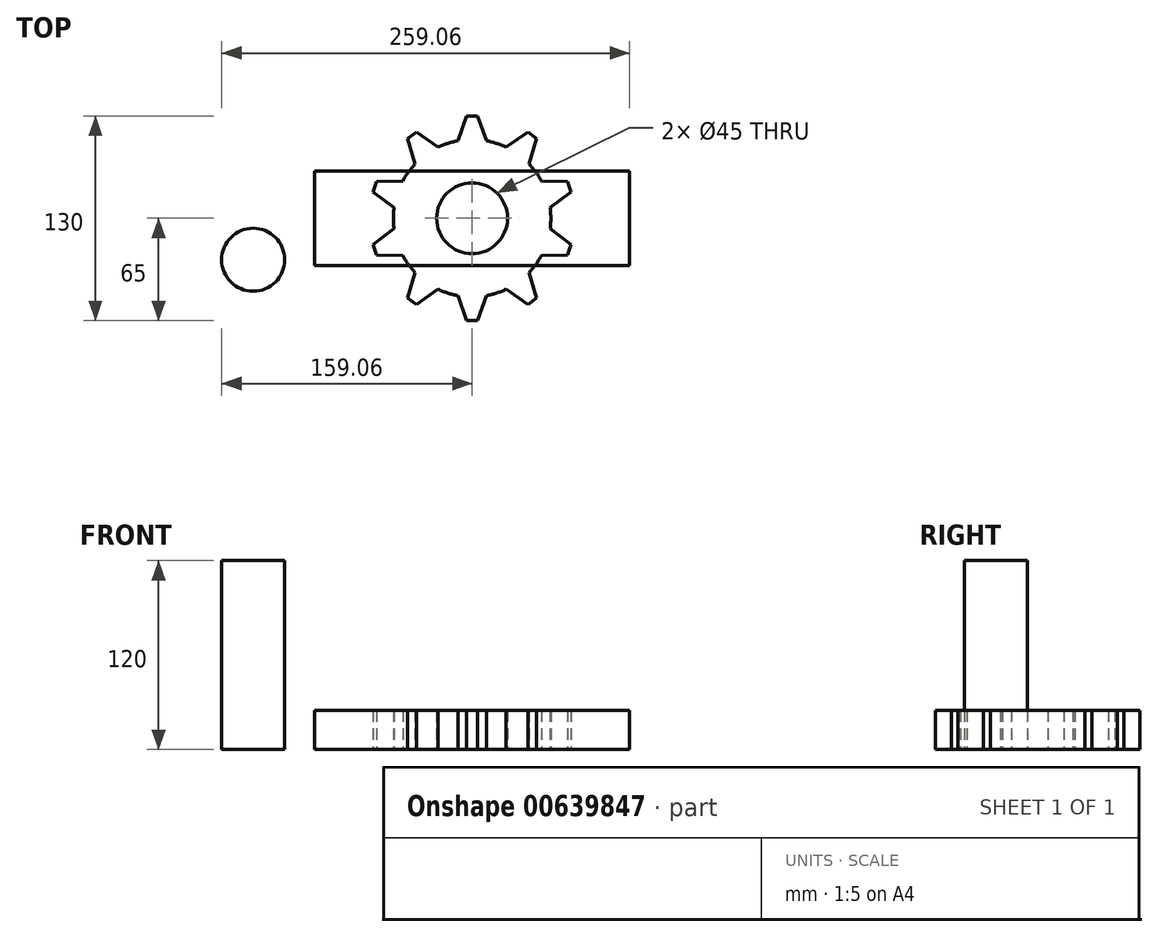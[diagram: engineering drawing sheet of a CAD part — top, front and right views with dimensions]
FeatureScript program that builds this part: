
annotation { "Feature Type Name" : "Feature", "Feature Type Description" : "" }
export const myFeature = defineFeature(function(context is Context, id is Id, definition is map)
    precondition{}
    {
        {
            var Q0;
            Q0=qCreatedBy(makeId("Top.planeOp"),FACE);
            var sketch = newSketch(context, id + "F0", { "sketchPlane" : qUnion([Q0])});
            skCircle(sketch, "E0", {"center": v(0, 0) * mm, "radius": 50 * mm});
            skLineSegment(sketch, "E1", {"start": v(0, 0) * mm, "end": v(0, 80) * mm, "construction": true});
            skLineSegment(sketch, "E2", {"start": v(0, 65) * mm, "end": v(3.5, 65) * mm});
            skLineSegment(sketch, "E3", {"start": v(3.5, 65) * mm, "end": v(9, 49.18) * mm});
            skLineSegment(sketch, "E4.MirrorCS", {"start": v(0, 65) * mm, "end": v(-3.5, 65) * mm});
            skLineSegment(sketch, "E5.MirrorCS", {"start": v(-3.5, 65) * mm, "end": v(-9, 49.18) * mm});
            skLineSegment(sketch, "E6.1.0", {"start": v(-41.04, 50.53) * mm, "end": v(-36.2, 34.5) * mm});
            skLineSegment(sketch, "E6.1.1", {"start": v(-38.2, 52.59) * mm, "end": v(-41.04, 50.53) * mm});
            skLineSegment(sketch, "E6.1.2", {"start": v(-38.2, 52.59) * mm, "end": v(-35.37, 54.64) * mm});
            skLineSegment(sketch, "E6.1.3", {"start": v(-35.37, 54.64) * mm, "end": v(-21.63, 45.08) * mm});
            skLineSegment(sketch, "E6.2.0", {"start": v(-62.9, 16.76) * mm, "end": v(-49.56, 6.64) * mm});
            skLineSegment(sketch, "E6.2.1", {"start": v(-61.82, 20.09) * mm, "end": v(-62.9, 16.76) * mm});
            skLineSegment(sketch, "E6.2.2", {"start": v(-61.82, 20.09) * mm, "end": v(-60.74, 23.41) * mm});
            skLineSegment(sketch, "E6.2.3", {"start": v(-60.74, 23.41) * mm, "end": v(-44, 23.76) * mm});
            skLineSegment(sketch, "E7.2.3.0", {"start": v(-60.74, -23.41) * mm, "end": v(-44, -23.76) * mm});
            skLineSegment(sketch, "E7.3.3.0", {"start": v(-61.82, -20.09) * mm, "end": v(-60.74, -23.41) * mm});
            skLineSegment(sketch, "E7.6.3.0", {"start": v(-61.82, -20.09) * mm, "end": v(-62.9, -16.76) * mm});
            skLineSegment(sketch, "E7.9.3.0", {"start": v(-62.9, -16.76) * mm, "end": v(-49.56, -6.64) * mm});
            skLineSegment(sketch, "E7.2.4.0", {"start": v(-35.37, -54.64) * mm, "end": v(-21.63, -45.08) * mm});
            skLineSegment(sketch, "E7.3.4.0", {"start": v(-38.2, -52.59) * mm, "end": v(-35.37, -54.64) * mm});
            skLineSegment(sketch, "E7.6.4.0", {"start": v(-38.2, -52.59) * mm, "end": v(-41.04, -50.53) * mm});
            skLineSegment(sketch, "E7.9.4.0", {"start": v(-41.04, -50.53) * mm, "end": v(-36.2, -34.5) * mm});
            skLineSegment(sketch, "E7.2.5.0", {"start": v(3.5, -65) * mm, "end": v(9, -49.18) * mm});
            skLineSegment(sketch, "E7.3.5.0", {"start": v(0, -65) * mm, "end": v(3.5, -65) * mm});
            skLineSegment(sketch, "E7.6.5.0", {"start": v(0, -65) * mm, "end": v(-3.5, -65) * mm});
            skLineSegment(sketch, "E7.9.5.0", {"start": v(-3.5, -65) * mm, "end": v(-9, -49.18) * mm});
            skLineSegment(sketch, "E7.2.6.0", {"start": v(41.04, -50.53) * mm, "end": v(36.2, -34.5) * mm});
            skLineSegment(sketch, "E7.3.6.0", {"start": v(38.2, -52.59) * mm, "end": v(41.04, -50.53) * mm});
            skLineSegment(sketch, "E7.6.6.0", {"start": v(38.2, -52.59) * mm, "end": v(35.37, -54.64) * mm});
            skLineSegment(sketch, "E7.9.6.0", {"start": v(35.37, -54.64) * mm, "end": v(21.63, -45.08) * mm});
            skLineSegment(sketch, "E7.2.7.0", {"start": v(62.9, -16.76) * mm, "end": v(49.56, -6.64) * mm});
            skLineSegment(sketch, "E7.3.7.0", {"start": v(61.82, -20.09) * mm, "end": v(62.9, -16.76) * mm});
            skLineSegment(sketch, "E7.6.7.0", {"start": v(61.82, -20.09) * mm, "end": v(60.74, -23.41) * mm});
            skLineSegment(sketch, "E7.9.7.0", {"start": v(60.74, -23.41) * mm, "end": v(44, -23.76) * mm});
            skLineSegment(sketch, "E7.2.8.0", {"start": v(60.74, 23.41) * mm, "end": v(44, 23.76) * mm});
            skLineSegment(sketch, "E7.3.8.0", {"start": v(61.82, 20.09) * mm, "end": v(60.74, 23.41) * mm});
            skLineSegment(sketch, "E7.6.8.0", {"start": v(61.82, 20.09) * mm, "end": v(62.9, 16.76) * mm});
            skLineSegment(sketch, "E7.9.8.0", {"start": v(62.9, 16.76) * mm, "end": v(49.56, 6.64) * mm});
            skLineSegment(sketch, "E7.2.9.0", {"start": v(35.37, 54.64) * mm, "end": v(21.63, 45.08) * mm});
            skLineSegment(sketch, "E7.3.9.0", {"start": v(38.2, 52.59) * mm, "end": v(35.37, 54.64) * mm});
            skLineSegment(sketch, "E7.6.9.0", {"start": v(38.2, 52.59) * mm, "end": v(41.04, 50.53) * mm});
            skLineSegment(sketch, "E7.9.9.0", {"start": v(41.04, 50.53) * mm, "end": v(36.2, 34.5) * mm});
            skSolve(sketch);
        }
        {
            var Q0;
            Q0=qCreatedBy(makeId("Top.planeOp"),FACE);
            var sketch = newSketch(context, id + "F1", { "sketchPlane" : qUnion([Q0])});
            skCircle(sketch, "E8", {"center": v(0, 0) * mm, "radius": 22.5 * mm});
            skSolve(sketch);
        }
        {
            var Q0;
            {var subQ0=sQuery(id+"F0.wireOp",EDGE,"E6.1.0");Q0=makeQuery(id+"F0.imprint","IMPRINT",FACE,{"disambiguationData":[TD([[makeQuery(id+"F0.imprint","IMPRINT",EDGE,{"derivedFrom":subQ0}),1.0]])]});}
            var Q1;
            {var subQ0=sQuery(id+"F0.wireOp",EDGE,"E6.2.0");Q1=makeQuery(id+"F0.imprint","IMPRINT",FACE,{"disambiguationData":[TD([[makeQuery(id+"F0.imprint","IMPRINT",EDGE,{"derivedFrom":subQ0}),1.0]])]});}
            var Q2;
            {var subQ0=sQuery(id+"F0.wireOp",EDGE,"E7.2.3.0");Q2=makeQuery(id+"F0.imprint","IMPRINT",FACE,{"disambiguationData":[TD([[makeQuery(id+"F0.imprint","IMPRINT",EDGE,{"derivedFrom":subQ0}),1.0]])]});}
            var Q3;
            {var subQ0=sQuery(id+"F0.wireOp",EDGE,"E7.2.4.0");Q3=makeQuery(id+"F0.imprint","IMPRINT",FACE,{"disambiguationData":[TD([[makeQuery(id+"F0.imprint","IMPRINT",EDGE,{"derivedFrom":subQ0}),1.0]])]});}
            var Q4;
            {var subQ0=sQuery(id+"F0.wireOp",EDGE,"E7.2.5.0");Q4=makeQuery(id+"F0.imprint","IMPRINT",FACE,{"disambiguationData":[TD([[makeQuery(id+"F0.imprint","IMPRINT",EDGE,{"derivedFrom":subQ0}),1.0]])]});}
            var Q5;
            {var subQ0=sQuery(id+"F0.wireOp",EDGE,"E7.2.6.0");Q5=makeQuery(id+"F0.imprint","IMPRINT",FACE,{"disambiguationData":[TD([[makeQuery(id+"F0.imprint","IMPRINT",EDGE,{"derivedFrom":subQ0}),1.0]])]});}
            var Q6;
            {var subQ0=sQuery(id+"F0.wireOp",EDGE,"E7.2.7.0");Q6=makeQuery(id+"F0.imprint","IMPRINT",FACE,{"disambiguationData":[TD([[makeQuery(id+"F0.imprint","IMPRINT",EDGE,{"derivedFrom":subQ0}),1.0]])]});}
            var Q7;
            {var subQ0=sQuery(id+"F0.wireOp",EDGE,"E7.2.8.0");Q7=makeQuery(id+"F0.imprint","IMPRINT",FACE,{"disambiguationData":[TD([[makeQuery(id+"F0.imprint","IMPRINT",EDGE,{"derivedFrom":subQ0}),1.0]])]});}
            var Q8;
            {var subQ0=sQuery(id+"F0.wireOp",EDGE,"E7.2.9.0");Q8=makeQuery(id+"F0.imprint","IMPRINT",FACE,{"disambiguationData":[TD([[makeQuery(id+"F0.imprint","IMPRINT",EDGE,{"derivedFrom":subQ0}),1.0]])]});}
            var Q9;
            Q9=makeQuery(id+"F0.imprint","IMPRINT",FACE,{"disambiguationData":[TD([[makeQuery(id+"F0.imprint","IMPRINT",EDGE,{"derivedFrom":sQuery(id+"F0.wireOp",EDGE,"E2")}),-1.0]])]});
            var Q10;
            {var subQ0=sQuery(id+"F0.wireOp",EDGE,"E0");var subQ8=makeQuery(id+"F0.imprint","INTERSECT",VERTEX,{"derivedFrom":[subQ0,sQuery(id+"F0.wireOp",EDGE,"E7.2.8.0")]});Q10=makeQuery(id+"F0.imprint","IMPRINT",FACE,{"disambiguationData":[TD([[makeQuery(id+"F0.imprint","IMPRINT",EDGE,{"disambiguationData":[TD([[subQ8,1.0]])],"derivedFrom":subQ0}),1.0]])]});}
            extrude(context, id + "F2", {"entities" : qUnion([Q0, Q1, Q2, Q3, Q4, Q5, Q6, Q7, Q8, Q9, Q10]), "depth" : 25 * mm, "offsetDistance" : 25 * mm});
        }
        {
            var Q0;
            Q0=makeQuery(id+"F1.imprint","IMPRINT",FACE,{"disambiguationData":[TD([[makeQuery(id+"F1.imprint","IMPRINT",EDGE,{"derivedFrom":sQuery(id+"F1.wireOp",EDGE,"E8")}),1.0]])]});
            extrude(context, id + "F3", {"entities" : qUnion([Q0]), "operationType" : NewBodyOperationType.REMOVE, "depth" : 25 * mm, "offsetDistance" : 25 * mm});
        }
        {
            var Q0;
            Q0=makeQuery(id+"F2.opExtrude","SWEPT_BODY",BODY,{"disambiguationData":[OSD([sQuery(id+"F0.wireOp",EDGE,"E0"),sQuery(id+"F0.wireOp",EDGE,"E2"),sQuery(id+"F0.wireOp",EDGE,"E3"),sQuery(id+"F0.wireOp",EDGE,"E4.MirrorCS"),sQuery(id+"F0.wireOp",EDGE,"E5.MirrorCS"),sQuery(id+"F0.wireOp",EDGE,"E6.1.0"),sQuery(id+"F0.wireOp",EDGE,"E6.1.1"),sQuery(id+"F0.wireOp",EDGE,"E6.1.2"),sQuery(id+"F0.wireOp",EDGE,"E6.1.3"),sQuery(id+"F0.wireOp",EDGE,"E6.2.0"),sQuery(id+"F0.wireOp",EDGE,"E6.2.1"),sQuery(id+"F0.wireOp",EDGE,"E6.2.2"),sQuery(id+"F0.wireOp",EDGE,"E6.2.3"),sQuery(id+"F0.wireOp",EDGE,"E7.2.3.0"),sQuery(id+"F0.wireOp",EDGE,"E7.3.3.0"),sQuery(id+"F0.wireOp",EDGE,"E7.6.3.0"),sQuery(id+"F0.wireOp",EDGE,"E7.9.3.0"),sQuery(id+"F0.wireOp",EDGE,"E7.2.4.0"),sQuery(id+"F0.wireOp",EDGE,"E7.3.4.0"),sQuery(id+"F0.wireOp",EDGE,"E7.6.4.0"),sQuery(id+"F0.wireOp",EDGE,"E7.9.4.0"),sQuery(id+"F0.wireOp",EDGE,"E7.2.5.0"),sQuery(id+"F0.wireOp",EDGE,"E7.3.5.0"),sQuery(id+"F0.wireOp",EDGE,"E7.6.5.0"),sQuery(id+"F0.wireOp",EDGE,"E7.9.5.0"),sQuery(id+"F0.wireOp",EDGE,"E7.2.6.0"),sQuery(id+"F0.wireOp",EDGE,"E7.3.6.0"),sQuery(id+"F0.wireOp",EDGE,"E7.6.6.0"),sQuery(id+"F0.wireOp",EDGE,"E7.9.6.0"),sQuery(id+"F0.wireOp",EDGE,"E7.2.7.0"),sQuery(id+"F0.wireOp",EDGE,"E7.3.7.0"),sQuery(id+"F0.wireOp",EDGE,"E7.6.7.0"),sQuery(id+"F0.wireOp",EDGE,"E7.9.7.0"),sQuery(id+"F0.wireOp",EDGE,"E7.2.8.0"),sQuery(id+"F0.wireOp",EDGE,"E7.3.8.0"),sQuery(id+"F0.wireOp",EDGE,"E7.6.8.0"),sQuery(id+"F0.wireOp",EDGE,"E7.9.8.0"),sQuery(id+"F0.wireOp",EDGE,"E7.2.9.0"),sQuery(id+"F0.wireOp",EDGE,"E7.3.9.0"),sQuery(id+"F0.wireOp",EDGE,"E7.6.9.0"),sQuery(id+"F0.wireOp",EDGE,"E7.9.9.0")])]});
            transform(context, id + "F4", {"entities" : qUnion([Q0]), "transformType" : TransformType.TRANSLATION_3D, "dx" : 0 * mm, "dy" : 0 * mm, "dz" : 0 * mm, "makeCopy" : true});
        }
        {
            var Q0;
            Q0=qCreatedBy(makeId("Top.planeOp"),FACE);
            var sketch = newSketch(context, id + "F5", { "sketchPlane" : qUnion([Q0])});
            skPoint(sketch, "E9.middle", {"position": v(0, 0) * mm});
            skLineSegment(sketch, "E10.bottom", {"start": v(100, -30) * mm, "end": v(-100, -30) * mm});
            skLineSegment(sketch, "E10.top", {"start": v(100, 30) * mm, "end": v(-100, 30) * mm});
            skLineSegment(sketch, "E10.left", {"start": v(100, -30) * mm, "end": v(100, 30) * mm});
            skLineSegment(sketch, "E10.right", {"start": v(-100, -30) * mm, "end": v(-100, 30) * mm});
            skSolve(sketch);
        }
        {
            var Q0;
            Q0=makeQuery(id+"F5.imprint","IMPRINT",FACE,{"disambiguationData":[TD([[makeQuery(id+"F5.imprint","IMPRINT",EDGE,{"derivedFrom":sQuery(id+"F5.wireOp",EDGE,"E10.bottom")}),-1.0]])]});
            extrude(context, id + "F6", {"entities" : qUnion([Q0]), "depth" : 25 * mm, "offsetDistance" : 25 * mm});
        }
        {
            var Q0;
            Q0=qCreatedBy(makeId("Top.planeOp"),FACE);
            var sketch = newSketch(context, id + "F7", { "sketchPlane" : qUnion([Q0])});
            skCircle(sketch, "E11", {"center": v(-139.06, -26.37) * mm, "radius": 20 * mm});
            skSolve(sketch);
        }
        {
            var Q0;
            Q0=makeQuery(id+"F7.imprint","IMPRINT",FACE,{"disambiguationData":[TD([[makeQuery(id+"F7.imprint","IMPRINT",EDGE,{"derivedFrom":sQuery(id+"F7.wireOp",EDGE,"E11")}),1.0]])]});
            extrude(context, id + "F8", {"entities" : qUnion([Q0]), "depth" : 120 * mm, "offsetDistance" : 25 * mm});
        }
    });
